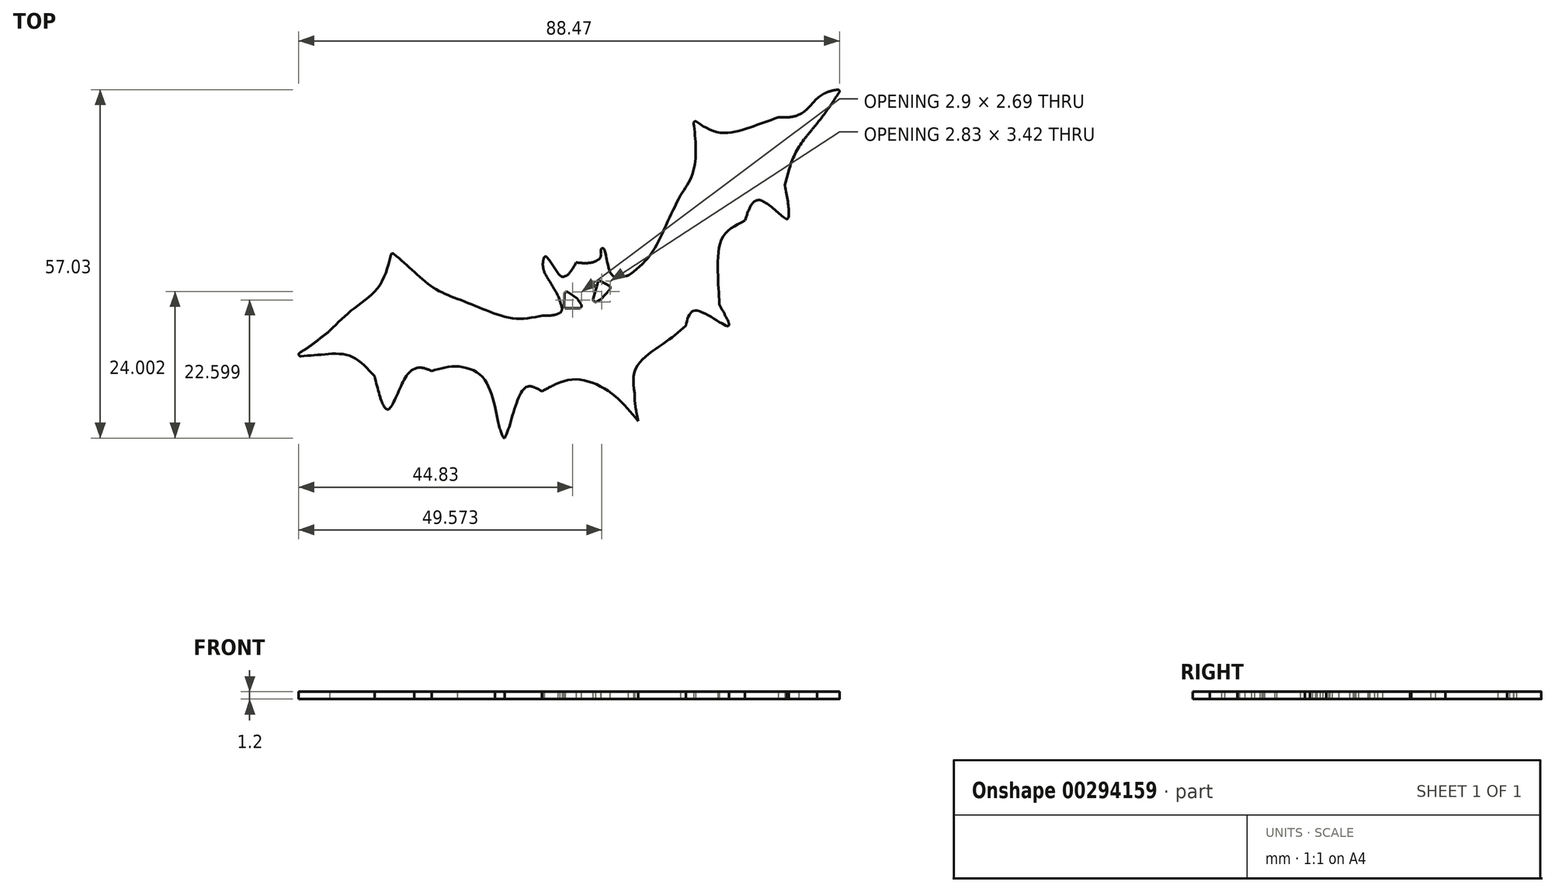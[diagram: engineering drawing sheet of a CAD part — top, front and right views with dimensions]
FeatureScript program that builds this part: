
annotation { "Feature Type Name" : "Feature", "Feature Type Description" : "" }
export const myFeature = defineFeature(function(context is Context, id is Id, definition is map)
    precondition{}
    {
        {
            var Q0;
            Q0=qCreatedBy(makeId("Top.planeOp"),FACE);
            var sketch = newSketch(context, id + "F0", { "sketchPlane" : qUnion([Q0])});
            skFitSpline(sketch, "E0", {"points": [v(-44.66, -16.52) * mm, v(-40.07, -16.2) * mm, v(-35.17, -16.39) * mm, v(-31.16, -19.7) * mm]});
            skFitSpline(sketch, "E1", {"points": [v(-31.16, -19.7) * mm, v(-28.88, -25.1) * mm, v(-25.34, -18.94) * mm, v(-22.1, -19) * mm]});
            skFitSpline(sketch, "E2", {"points": [v(-22.1, -19) * mm, v(-18.1, -18.24) * mm, v(-13.91, -19.85) * mm, v(-11.75, -24.76) * mm]});
            skFitSpline(sketch, "E3", {"points": [v(-11.75, -24.76) * mm, v(-9.97, -29.92) * mm, v(-6.73, -21.78) * mm, v(-3.78, -22.2) * mm]});
            skFitSpline(sketch, "E4", {"points": [v(-3.78, -22.2) * mm, v(1.64, -20.24) * mm, v(7.6, -22.53) * mm, v(11.97, -27.04) * mm]});
            skFitSpline(sketch, "E5", {"points": [v(11.97, -27.04) * mm, v(11.83, -20.48) * mm, v(16.33, -16.23) * mm, v(20.02, -13.08) * mm]});
            skFitSpline(sketch, "E6", {"points": [v(20.02, -13.08) * mm, v(21.71, -10.4) * mm, v(26.97, -13.12) * mm, v(24.97, -8.1) * mm]});
            skFitSpline(sketch, "E7", {"points": [v(24.97, -8.1) * mm, v(24.74, -3.06) * mm, v(25.53, 2.93) * mm, v(29.14, 5.6) * mm]});
            skFitSpline(sketch, "E8", {"points": [v(29.14, 5.6) * mm, v(31.56, 8.97) * mm, v(36.56, 5.58) * mm, v(36.37, 11.62) * mm]});
            skFitSpline(sketch, "E9", {"points": [v(36.37, 11.62) * mm, v(38.29, 17.6) * mm, v(41.67, 22.45) * mm, v(44.95, 27.17) * mm]});
            skFitSpline(sketch, "E10", {"points": [v(44.95, 27.17) * mm, v(41.5, 26.04) * mm, v(38.47, 23.2) * mm, v(34.87, 22.65) * mm]});
            skFitSpline(sketch, "E11", {"points": [v(34.87, 22.65) * mm, v(30.24, 21) * mm, v(25.19, 20.17) * mm, v(20.61, 22.6) * mm]});
            skFitSpline(sketch, "E12", {"points": [v(20.61, 22.6) * mm, v(21.08, 18.15) * mm, v(20.62, 13.45) * mm, v(18.6, 9.75) * mm]});
            skFitSpline(sketch, "E13", {"points": [v(18.6, 9.75) * mm, v(16.28, 4.97) * mm, v(13.73, 0.08) * mm, v(10.24, -3.27) * mm]});
            skFitSpline(sketch, "E14", {"points": [v(10.24, -3.27) * mm, v(7.72, -3.18) * mm, v(6.45, 1.01) * mm, v(4.8, 3.2) * mm]});
            skFitSpline(sketch, "E15", {"points": [v(4.8, 3.2) * mm, v(5.52, -0.34) * mm, v(4, -1.16) * mm, v(1.62, -1.07) * mm]});
            skFitSpline(sketch, "E16", {"points": [v(1.62, -1.07) * mm, v(-0.33, -3.45) * mm, v(-1.87, -1.73) * mm, v(-3.42, 0.37) * mm]});
            skFitSpline(sketch, "E17", {"points": [v(-3.42, 0.37) * mm, v(-3.7, -2.72) * mm, v(-0.8, -9.01) * mm, v(-3.63, -9.8) * mm]});
            skFitSpline(sketch, "E18", {"points": [v(-3.63, -9.8) * mm, v(-8.35, -10.25) * mm, v(-13.1, -8.84) * mm, v(-17.6, -7.04) * mm]});
            skFitSpline(sketch, "E19", {"points": [v(-17.6, -7.04) * mm, v(-21.47, -5.27) * mm, v(-24.98, -2.36) * mm, v(-28.38, 0.64) * mm]});
            skFitSpline(sketch, "E20", {"points": [v(-28.38, 0.64) * mm, v(-30.5, -5.08) * mm, v(-34.68, -8.74) * mm, v(-38.48, -12.27) * mm]});
            skFitSpline(sketch, "E21", {"points": [v(-38.48, -12.27) * mm, v(-40.47, -13.84) * mm, v(-42.5, -15.31) * mm, v(-44.62, -16.58) * mm]});
            skFitSpline(sketch, "E22", {"points": [v(-44.95, -16.65) * mm, v(-40.36, -16.32) * mm, v(-35.46, -16.52) * mm, v(-31.44, -19.84) * mm]});
            skFitSpline(sketch, "E23", {"points": [v(-31.44, -19.84) * mm, v(-29.17, -25.23) * mm, v(-25.63, -19.07) * mm, v(-22.39, -19.12) * mm]});
            skFitSpline(sketch, "E24", {"points": [v(-22.39, -19.12) * mm, v(-18.4, -18.37) * mm, v(-14.2, -19.98) * mm, v(-12.04, -24.89) * mm]});
            skFitSpline(sketch, "E25", {"points": [v(-12.04, -24.89) * mm, v(-10.26, -30.05) * mm, v(-7.02, -21.91) * mm, v(-4.07, -22.32) * mm]});
            skFitSpline(sketch, "E26", {"points": [v(-4.07, -22.32) * mm, v(1.35, -20.36) * mm, v(7.32, -22.66) * mm, v(11.68, -27.17) * mm]});
            skFitSpline(sketch, "E27", {"points": [v(11.68, -27.17) * mm, v(11.54, -20.61) * mm, v(16.04, -16.36) * mm, v(19.73, -13.2) * mm]});
            skFitSpline(sketch, "E28", {"points": [v(19.73, -13.2) * mm, v(21.42, -10.54) * mm, v(26.68, -13.25) * mm, v(24.68, -8.23) * mm]});
            skFitSpline(sketch, "E29", {"points": [v(24.68, -8.23) * mm, v(24.45, -3.18) * mm, v(25.24, 2.8) * mm, v(28.85, 5.48) * mm]});
            skFitSpline(sketch, "E30", {"points": [v(28.85, 5.48) * mm, v(31.27, 8.84) * mm, v(36.27, 5.45) * mm, v(36.08, 11.49) * mm]});
            skFitSpline(sketch, "E31", {"points": [v(36.08, 11.49) * mm, v(38, 17.47) * mm, v(41.38, 22.32) * mm, v(44.66, 27.04) * mm]});
            skFitSpline(sketch, "E32", {"points": [v(44.66, 27.04) * mm, v(41.2, 25.91) * mm, v(38.18, 23.07) * mm, v(34.58, 22.53) * mm]});
            skFitSpline(sketch, "E33", {"points": [v(34.58, 22.53) * mm, v(29.95, 20.86) * mm, v(24.9, 20.04) * mm, v(20.33, 22.47) * mm]});
            skFitSpline(sketch, "E34", {"points": [v(20.33, 22.47) * mm, v(20.8, 18.02) * mm, v(20.33, 13.32) * mm, v(18.3, 9.62) * mm]});
            skFitSpline(sketch, "E35", {"points": [v(18.3, 9.62) * mm, v(15.99, 4.84) * mm, v(13.45, -0.05) * mm, v(9.96, -3.4) * mm]});
            skFitSpline(sketch, "E36", {"points": [v(9.96, -3.4) * mm, v(7.43, -3.31) * mm, v(6.16, 0.88) * mm, v(4.5, 3.08) * mm]});
            skFitSpline(sketch, "E37", {"points": [v(4.5, 3.08) * mm, v(5.23, -0.46) * mm, v(3.71, -1.3) * mm, v(1.33, -1.2) * mm]});
            skFitSpline(sketch, "E38", {"points": [v(1.33, -1.2) * mm, v(-0.62, -3.58) * mm, v(-2.16, -1.86) * mm, v(-3.71, 0.24) * mm]});
            skFitSpline(sketch, "E39", {"points": [v(-3.71, 0.24) * mm, v(-4, -2.85) * mm, v(-1.1, -9.14) * mm, v(-3.92, -9.92) * mm]});
            skFitSpline(sketch, "E40", {"points": [v(-3.92, -9.92) * mm, v(-8.64, -10.38) * mm, v(-13.38, -8.97) * mm, v(-17.88, -7.17) * mm]});
            skFitSpline(sketch, "E41", {"points": [v(-17.88, -7.17) * mm, v(-21.76, -5.4) * mm, v(-25.27, -2.48) * mm, v(-28.67, 0.5) * mm]});
            skFitSpline(sketch, "E42", {"points": [v(-28.67, 0.5) * mm, v(-30.79, -5.21) * mm, v(-34.97, -8.87) * mm, v(-38.77, -12.4) * mm]});
            skFitSpline(sketch, "E43", {"points": [v(-38.77, -12.4) * mm, v(-40.76, -13.97) * mm, v(-42.8, -15.44) * mm, v(-44.9, -16.71) * mm]});
            skFitSpline(sketch, "E44", {"points": [v(-44.66, -14.8) * mm, v(-40.11, -14.5) * mm, v(-35.26, -14.67) * mm, v(-31.27, -17.76) * mm]});
            skFitSpline(sketch, "E45", {"points": [v(-31.27, -17.76) * mm, v(-29.02, -22.79) * mm, v(-25.5, -17.05) * mm, v(-22.3, -17.1) * mm]});
            skFitSpline(sketch, "E46", {"points": [v(-22.3, -17.1) * mm, v(-18.33, -16.4) * mm, v(-14.18, -17.9) * mm, v(-12.04, -22.46) * mm]});
            skFitSpline(sketch, "E47", {"points": [v(-12.04, -22.46) * mm, v(-10.27, -27.27) * mm, v(-7.05, -19.7) * mm, v(-4.13, -20.07) * mm]});
            skFitSpline(sketch, "E48", {"points": [v(-4.13, -20.07) * mm, v(1.24, -18.25) * mm, v(7.16, -20.39) * mm, v(11.48, -24.59) * mm]});
            skFitSpline(sketch, "E49", {"points": [v(11.48, -24.59) * mm, v(11.34, -18.48) * mm, v(15.8, -14.53) * mm, v(19.46, -11.59) * mm]});
            skFitSpline(sketch, "E50", {"points": [v(19.46, -11.59) * mm, v(21.14, -9.1) * mm, v(26.35, -11.63) * mm, v(24.37, -6.96) * mm]});
            skFitSpline(sketch, "E51", {"points": [v(24.37, -6.96) * mm, v(24.14, -2.26) * mm, v(24.92, 3.31) * mm, v(28.5, 5.8) * mm]});
            skFitSpline(sketch, "E52", {"points": [v(28.5, 5.8) * mm, v(30.9, 8.94) * mm, v(35.86, 5.78) * mm, v(35.67, 11.4) * mm]});
            skFitSpline(sketch, "E53", {"points": [v(35.67, 11.4) * mm, v(37.57, 16.97) * mm, v(40.93, 21.49) * mm, v(44.18, 25.88) * mm]});
            skFitSpline(sketch, "E54", {"points": [v(44.18, 25.88) * mm, v(40.75, 24.83) * mm, v(37.75, 22.18) * mm, v(34.18, 21.68) * mm]});
            skFitSpline(sketch, "E55", {"points": [v(34.18, 21.68) * mm, v(29.6, 20.13) * mm, v(24.59, 19.36) * mm, v(20.05, 21.63) * mm]});
            skFitSpline(sketch, "E56", {"points": [v(20.05, 21.63) * mm, v(20.52, 17.48) * mm, v(20.06, 13.1) * mm, v(18.05, 9.66) * mm]});
            skFitSpline(sketch, "E57", {"points": [v(18.05, 9.66) * mm, v(15.75, 5.2) * mm, v(13.23, 0.66) * mm, v(9.77, -2.46) * mm]});
            skFitSpline(sketch, "E58", {"points": [v(9.77, -2.46) * mm, v(7.27, -2.38) * mm, v(6, 1.53) * mm, v(4.37, 3.57) * mm]});
            skFitSpline(sketch, "E59", {"points": [v(4.37, 3.57) * mm, v(5.09, 0.27) * mm, v(3.58, -0.5) * mm, v(1.22, -0.41) * mm]});
            skFitSpline(sketch, "E60", {"points": [v(1.22, -0.41) * mm, v(-0.71, -2.62) * mm, v(-2.23, -1.02) * mm, v(-3.78, 0.93) * mm]});
            skFitSpline(sketch, "E61", {"points": [v(-3.78, 0.93) * mm, v(-4.05, -1.95) * mm, v(-1.18, -7.8) * mm, v(-3.99, -8.53) * mm]});
            skFitSpline(sketch, "E62", {"points": [v(-3.99, -8.53) * mm, v(-8.66, -8.96) * mm, v(-13.36, -7.65) * mm, v(-17.82, -5.97) * mm]});
            skFitSpline(sketch, "E63", {"points": [v(-17.82, -5.97) * mm, v(-21.67, -4.32) * mm, v(-25.15, -1.6) * mm, v(-28.52, 1.18) * mm]});
            skFitSpline(sketch, "E64", {"points": [v(-28.52, 1.18) * mm, v(-30.62, -4.15) * mm, v(-34.77, -7.55) * mm, v(-38.53, -10.83) * mm]});
            skFitSpline(sketch, "E65", {"points": [v(-38.53, -10.83) * mm, v(-40.5, -12.3) * mm, v(-42.53, -13.67) * mm, v(-44.62, -14.85) * mm]});
            skLineSegment(sketch, "E66", {"start": v(4.08, -8.06) * mm, "end": v(5.55, -7.3) * mm});
            skLineSegment(sketch, "E67", {"start": v(5.55, -7.3) * mm, "end": v(7.37, -5.26) * mm});
            skLineSegment(sketch, "E68", {"start": v(7.37, -5.26) * mm, "end": v(5.2, -4.06) * mm});
            skLineSegment(sketch, "E69", {"start": v(5.2, -4.06) * mm, "end": v(4.08, -8.06) * mm});
            skLineSegment(sketch, "E70", {"start": v(2.8, -8.72) * mm, "end": v(1.74, -7.19) * mm});
            skLineSegment(sketch, "E71", {"start": v(1.74, -7.19) * mm, "end": v(-0.36, -5.66) * mm});
            skLineSegment(sketch, "E72", {"start": v(-0.36, -5.66) * mm, "end": v(-0.5, -8.72) * mm});
            skLineSegment(sketch, "E73", {"start": v(-0.5, -8.72) * mm, "end": v(2.8, -8.72) * mm});
            skSolve(sketch);
        }
        {
            var Q0;
            {var subQ21=sQuery(id+"F0.wireOp",EDGE,"E13");Q0=makeQuery(id+"F0.imprint","IMPRINT",FACE,{"disambiguationData":[TD([[makeQuery(id+"F0.imprint","IMPRINT",EDGE,{"derivedFrom":subQ21}),1.0]])]});}
            var Q1;
            {var subQ4=sQuery(id+"F0.wireOp",EDGE,"E2");Q1=makeQuery(id+"F0.imprint","IMPRINT",FACE,{"disambiguationData":[TD([[makeQuery(id+"F0.imprint","IMPRINT",EDGE,{"derivedFrom":subQ4}),1.0]])]});}
            var Q2;
            {var subQ6=sQuery(id+"F0.wireOp",EDGE,"E7");Q2=makeQuery(id+"F0.imprint","IMPRINT",FACE,{"disambiguationData":[TD([[makeQuery(id+"F0.imprint","IMPRINT",EDGE,{"derivedFrom":subQ6}),1.0]])]});}
            var Q3;
            {var subQ9=sQuery(id+"F0.wireOp",EDGE,"E51");Q3=makeQuery(id+"F0.imprint","IMPRINT",FACE,{"disambiguationData":[TD([[makeQuery(id+"F0.imprint","IMPRINT",EDGE,{"derivedFrom":subQ9}),-1.0]])]});}
            var Q4;
            {var subQ0=sQuery(id+"F0.wireOp",EDGE,"E32");var subQ10=sQuery(id+"F0.wireOp",EDGE,"E10");var subQ11=makeQuery(id+"F0.imprint","INTERSECT",VERTEX,{"disambiguationData":[OD(0.0)],"derivedFrom":[subQ10,subQ0]});Q4=makeQuery(id+"F0.imprint","IMPRINT",FACE,{"disambiguationData":[TD([[makeQuery(id+"F0.imprint","IMPRINT",EDGE,{"disambiguationData":[TD([[subQ11,-1.0]])],"derivedFrom":subQ10}),1.0]])]});}
            var Q5;
            {var subQ3=sQuery(id+"F0.wireOp",EDGE,"E10");var subQ5=sQuery(id+"F0.wireOp",EDGE,"E9");var subQ6=makeQuery(id+"F0.imprint","INTERSECT",VERTEX,{"derivedFrom":[subQ5,subQ3]});Q5=makeQuery(id+"F0.imprint","IMPRINT",FACE,{"disambiguationData":[TD([[makeQuery(id+"F0.imprint","IMPRINT",EDGE,{"disambiguationData":[TD([[subQ6,1.0]])],"derivedFrom":subQ5}),1.0]])]});}
            var Q6;
            {var subQ0=sQuery(id+"F0.wireOp",EDGE,"E53");var subQ1=sQuery(id+"F0.wireOp",EDGE,"E9");var subQ2=makeQuery(id+"F0.imprint","INTERSECT",VERTEX,{"derivedFrom":[subQ1,subQ0]});Q6=makeQuery(id+"F0.imprint","IMPRINT",FACE,{"disambiguationData":[TD([[makeQuery(id+"F0.imprint","IMPRINT",EDGE,{"disambiguationData":[TD([[subQ2,-1.0]])],"derivedFrom":subQ1}),1.0]])]});}
            var Q7;
            {var subQ3=sQuery(id+"F0.wireOp",EDGE,"E43");var subQ6=sQuery(id+"F0.wireOp",EDGE,"E0");var subQ10=makeQuery(id+"F0.imprint","INTERSECT",VERTEX,{"derivedFrom":[subQ6,subQ3]});Q7=makeQuery(id+"F0.imprint","IMPRINT",FACE,{"disambiguationData":[TD([[makeQuery(id+"F0.imprint","IMPRINT",EDGE,{"disambiguationData":[TD([[subQ10,-1.0]])],"derivedFrom":subQ6}),-1.0]])]});}
            var Q8;
            {var subQ0=sQuery(id+"F0.wireOp",EDGE,"E43");var subQ1=sQuery(id+"F0.wireOp",EDGE,"E0");var subQ2=makeQuery(id+"F0.imprint","INTERSECT",VERTEX,{"derivedFrom":[subQ1,subQ0]});Q8=makeQuery(id+"F0.imprint","IMPRINT",FACE,{"disambiguationData":[TD([[makeQuery(id+"F0.imprint","IMPRINT",EDGE,{"disambiguationData":[TD([[subQ2,-1.0]])],"derivedFrom":subQ1}),1.0]])]});}
            var Q9;
            {var subQ0=sQuery(id+"F0.wireOp",EDGE,"E42");Q9=makeQuery(id+"F0.imprint","IMPRINT",FACE,{"disambiguationData":[TD([[makeQuery(id+"F0.imprint","IMPRINT",EDGE,{"derivedFrom":subQ0}),1.0]])]});}
            var Q10;
            {var subQ0=sQuery(id+"F0.wireOp",EDGE,"E29");var subQ1=sQuery(id+"F0.wireOp",EDGE,"E28");var subQ2=makeQuery(id+"F0.imprint","INTERSECT",VERTEX,{"derivedFrom":[subQ1,subQ0]});Q10=makeQuery(id+"F0.imprint","IMPRINT",FACE,{"disambiguationData":[TD([[makeQuery(id+"F0.imprint","IMPRINT",EDGE,{"disambiguationData":[TD([[subQ2,1.0]])],"derivedFrom":subQ1}),-1.0]])]});}
            var Q11;
            {var subQ0=sQuery(id+"F0.wireOp",EDGE,"E26");Q11=makeQuery(id+"F0.imprint","IMPRINT",FACE,{"disambiguationData":[TD([[makeQuery(id+"F0.imprint","IMPRINT",EDGE,{"derivedFrom":subQ0}),1.0]])]});}
            extrude(context, id + "F1", {"entities" : qUnion([Q0, Q1, Q2, Q3, Q4, Q5, Q6, Q7, Q8, Q9, Q10, Q11]), "depth" : 1.2 * mm});
        }
        {
            var Q0;
            Q0=makeQuery(id+"F1.opExtrude","SWEPT_EDGE",EDGE,{"disambiguationData":[OSD([sQuery(id+"F0.wireOp",EDGE,"E41"),sQuery(id+"F0.wireOp",EDGE,"E42")])]});
            var Q1;
            Q1=makeQuery(id+"F1.opExtrude","SWEPT_EDGE",EDGE,{"disambiguationData":[OSD([sQuery(id+"F0.wireOp",EDGE,"E12"),sQuery(id+"F0.wireOp",EDGE,"E33")])]});
            var Q2;
            Q2=makeQuery(id+"F1.opExtrude","SWEPT_EDGE",EDGE,{"disambiguationData":[OSD([sQuery(id+"F0.wireOp",EDGE,"E17"),sQuery(id+"F0.wireOp",EDGE,"E38")])]});
            var Q3;
            Q3=makeQuery(id+"F1.opExtrude","SWEPT_EDGE",EDGE,{"disambiguationData":[OSD([sQuery(id+"F0.wireOp",EDGE,"E15"),sQuery(id+"F0.wireOp",EDGE,"E36")])]});
            var Q4;
            Q4=makeQuery(id+"F1.opExtrude","SWEPT_EDGE",EDGE,{"disambiguationData":[OSD([sQuery(id+"F0.wireOp",EDGE,"E9"),sQuery(id+"F0.wireOp",EDGE,"E10")])]});
            var Q5;
            Q5=makeQuery(id+"F1.opExtrude","SWEPT_EDGE",EDGE,{"disambiguationData":[OSD([sQuery(id+"F0.wireOp",EDGE,"E22"),sQuery(id+"F0.wireOp",EDGE,"E43")])]});
            var Q6;
            Q6=makeQuery(id+"F1.opExtrude","SWEPT_EDGE",EDGE,{"disambiguationData":[OSD([sQuery(id+"F0.wireOp",EDGE,"E4"),sQuery(id+"F0.wireOp",EDGE,"E27")])]});
            fillet(context, id + "F2", {"entities" : qUnion([Q0, Q1, Q2, Q3, Q4, Q5, Q6]), "radius" : 0.3 * mm, "tangentPropagation" : true, "allowEdgeOverflow" : false});
        }
        {
            var Q0;
            Q0=makeQuery(id+"F1.opExtrude","SWEPT_EDGE",EDGE,{"disambiguationData":[OSD([sQuery(id+"F0.wireOp",EDGE,"E35"),sQuery(id+"F0.wireOp",EDGE,"E36")])]});
            var Q1;
            Q1=makeQuery(id+"F1.opExtrude","SWEPT_EDGE",EDGE,{"disambiguationData":[OSD([sQuery(id+"F0.wireOp",EDGE,"E13"),sQuery(id+"F0.wireOp",EDGE,"E14")])]});
            fillet(context, id + "F3", {"entities" : qUnion([Q0, Q1]), "radius" : 1 * mm, "tangentPropagation" : true, "allowEdgeOverflow" : false});
        }
        {
            var Q0;
            Q0=makeQuery(id+"F1.opExtrude","SWEPT_EDGE",EDGE,{"disambiguationData":[OSD([sQuery(id+"F0.wireOp",EDGE,"E67"),sQuery(id+"F0.wireOp",EDGE,"E68")])]});
            var Q1;
            Q1=makeQuery(id+"F1.opExtrude","SWEPT_EDGE",EDGE,{"disambiguationData":[OSD([sQuery(id+"F0.wireOp",EDGE,"E68"),sQuery(id+"F0.wireOp",EDGE,"E69")])]});
            var Q2;
            Q2=makeQuery(id+"F1.opExtrude","SWEPT_EDGE",EDGE,{"disambiguationData":[OSD([sQuery(id+"F0.wireOp",EDGE,"E66"),sQuery(id+"F0.wireOp",EDGE,"E69")])]});
            var Q3;
            Q3=makeQuery(id+"F1.opExtrude","SWEPT_EDGE",EDGE,{"disambiguationData":[OSD([sQuery(id+"F0.wireOp",EDGE,"E72"),sQuery(id+"F0.wireOp",EDGE,"E73")])]});
            var Q4;
            Q4=makeQuery(id+"F1.opExtrude","SWEPT_EDGE",EDGE,{"disambiguationData":[OSD([sQuery(id+"F0.wireOp",EDGE,"E70"),sQuery(id+"F0.wireOp",EDGE,"E73")])]});
            var Q5;
            Q5=makeQuery(id+"F1.opExtrude","SWEPT_EDGE",EDGE,{"disambiguationData":[OSD([sQuery(id+"F0.wireOp",EDGE,"E71"),sQuery(id+"F0.wireOp",EDGE,"E72")])]});
            var Q6;
            Q6=makeQuery(id+"F1.opExtrude","SWEPT_EDGE",EDGE,{"disambiguationData":[OSD([sQuery(id+"F0.wireOp",EDGE,"E66"),sQuery(id+"F0.wireOp",EDGE,"E67")])]});
            var Q7;
            Q7=makeQuery(id+"F1.opExtrude","SWEPT_EDGE",EDGE,{"disambiguationData":[OSD([sQuery(id+"F0.wireOp",EDGE,"E70"),sQuery(id+"F0.wireOp",EDGE,"E71")])]});
            fillet(context, id + "F4", {"entities" : qUnion([Q0, Q1, Q2, Q3, Q4, Q5, Q6, Q7]), "radius" : 0.4 * mm, "tangentPropagation" : true, "allowEdgeOverflow" : false});
        }
    });
